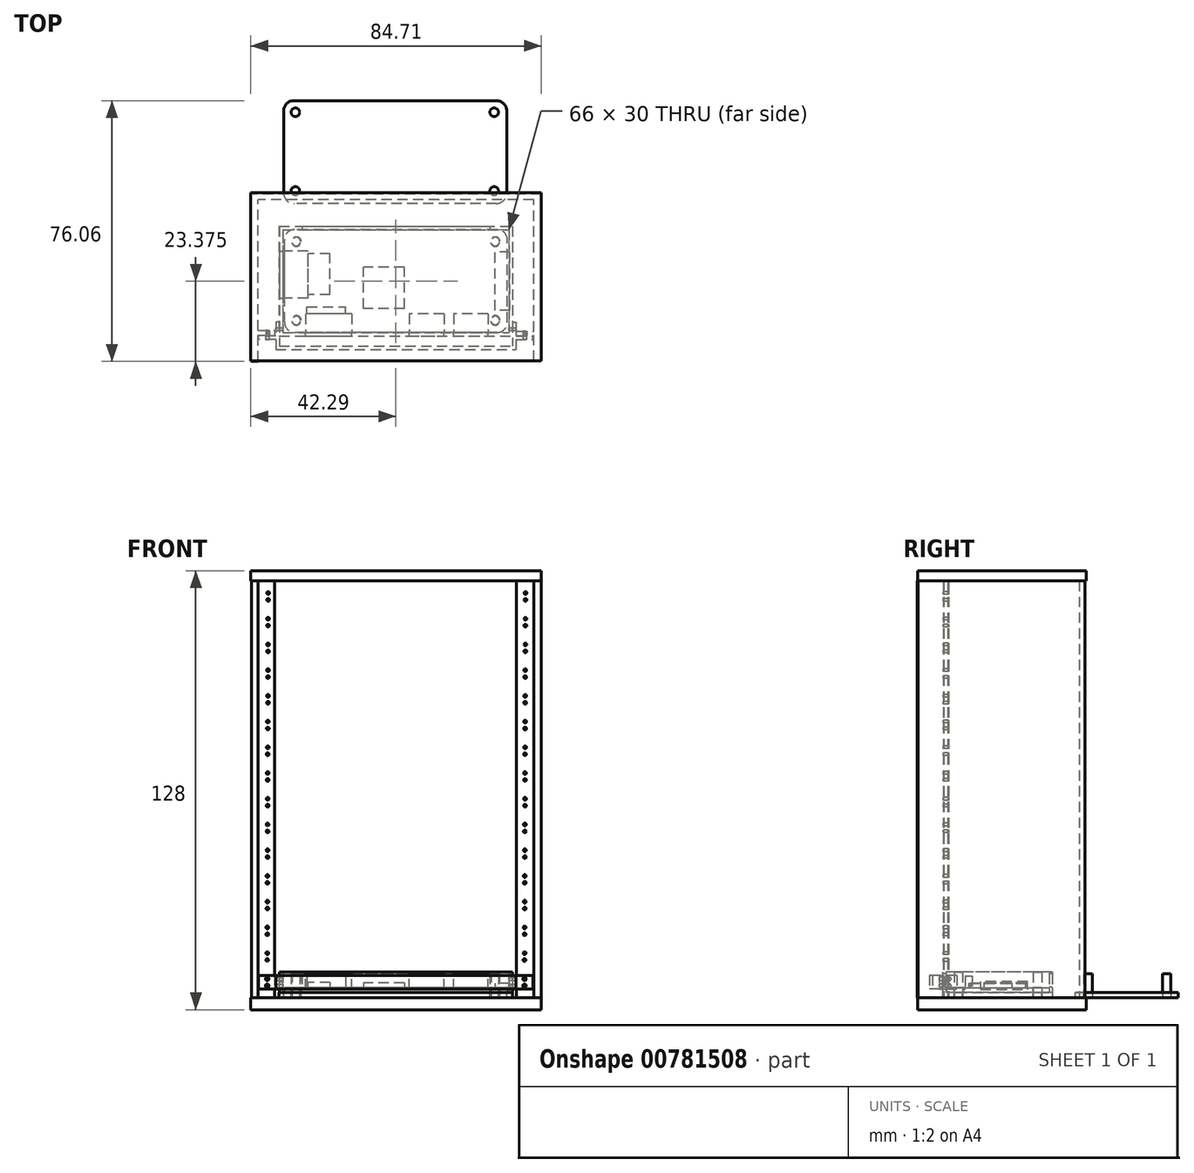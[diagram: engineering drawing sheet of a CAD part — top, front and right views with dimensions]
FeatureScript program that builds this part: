
annotation { "Feature Type Name" : "Feature", "Feature Type Description" : "" }
export const myFeature = defineFeature(function(context is Context, id is Id, definition is map)
    precondition{}
    {
        {
            var Q0;
            Q0=qCreatedBy(makeId("Top.planeOp"),FACE);
            var sketch = newSketch(context, id + "F0", { "sketchPlane" : qUnion([Q0])});
            skLineSegment(sketch, "E0.bottom", {"start": v(29.5, -15) * mm, "end": v(-29.5, -15) * mm});
            skLineSegment(sketch, "E0.top", {"start": v(29.5, 15) * mm, "end": v(-29.5, 15) * mm});
            skLineSegment(sketch, "E0.left", {"start": v(32.5, -12) * mm, "end": v(32.5, 12) * mm});
            skLineSegment(sketch, "E0.right", {"start": v(-32.5, -12) * mm, "end": v(-32.5, 12) * mm});
            skPoint(sketch, "E0.middle", {"position": v(0, 0) * mm});
            skCircle(sketch, "E1", {"center": v(-28.98, 11.47) * mm, "radius": 1.38 * mm});
            skCircle(sketch, "E2", {"center": v(28.98, 11.47) * mm, "radius": 1.38 * mm});
            skCircle(sketch, "E3", {"center": v(-28.98, -11.47) * mm, "radius": 1.38 * mm});
            skCircle(sketch, "E4", {"center": v(28.98, -11.47) * mm, "radius": 1.38 * mm});
            skPoint(sketch, "E5.visualSharp", {"position": v(-32.5, 15) * mm});
            skArc(sketch, "E5.filletArc", {"start": v(-29.5, 15) * mm, "mid": v(-31.62, 14.12) * mm, "end": v(-32.5, 12) * mm});
            skPoint(sketch, "E6.visualSharp", {"position": v(32.5, 15) * mm});
            skArc(sketch, "E6.filletArc", {"start": v(32.5, 12) * mm, "mid": v(31.62, 14.12) * mm, "end": v(29.5, 15) * mm});
            skPoint(sketch, "E7.visualSharp", {"position": v(32.5, -15) * mm});
            skArc(sketch, "E7.filletArc", {"start": v(29.5, -15) * mm, "mid": v(31.62, -14.12) * mm, "end": v(32.5, -12) * mm});
            skPoint(sketch, "E8.visualSharp", {"position": v(-32.5, -15) * mm});
            skArc(sketch, "E8.filletArc", {"start": v(-32.5, -12) * mm, "mid": v(-31.62, -14.12) * mm, "end": v(-29.5, -15) * mm});
            skSolve(sketch);
        }
        {
            var Q0;
            Q0=qSketchRegion(id+"F0",true);
            extrude(context, id + "F1", {"entities" : qUnion([Q0]), "depth" : 1.4 * mm});
        }
        {
            var Q0;
            Q0=makeQuery(id+"F1.opExtrude","CAP_FACE",FACE,{"disambiguationData":[OSD([sQuery(id+"F0.wireOp",EDGE,"E0.bottom"),sQuery(id+"F0.wireOp",EDGE,"E0.top"),sQuery(id+"F0.wireOp",EDGE,"E0.left"),sQuery(id+"F0.wireOp",EDGE,"E0.right"),sQuery(id+"F0.wireOp",EDGE,"E1"),sQuery(id+"F0.wireOp",EDGE,"E2"),sQuery(id+"F0.wireOp",EDGE,"E3"),sQuery(id+"F0.wireOp",EDGE,"E4"),sQuery(id+"F0.wireOp",EDGE,"E5.filletArc"),sQuery(id+"F0.wireOp",EDGE,"E6.filletArc"),sQuery(id+"F0.wireOp",EDGE,"E7.filletArc"),sQuery(id+"F0.wireOp",EDGE,"E8.filletArc")])],"isStart":false});
            var sketch = newSketch(context, id + "F2", { "sketchPlane" : qUnion([Q0])});
            skLineSegment(sketch, "E9.bottom", {"start": v(2.5, -8) * mm, "end": v(-9.5, -8) * mm});
            skLineSegment(sketch, "E9.top", {"start": v(2.5, 4) * mm, "end": v(-9.5, 4) * mm});
            skLineSegment(sketch, "E9.left", {"start": v(2.5, -8) * mm, "end": v(2.5, 4) * mm});
            skLineSegment(sketch, "E9.right", {"start": v(-9.5, -8) * mm, "end": v(-9.5, 4) * mm});
            skPoint(sketch, "E9.middle", {"position": v(-3.5, -2) * mm});
            skLineSegment(sketch, "E10.bottom", {"start": v(33.25, -8.5) * mm, "end": v(28.85, -8.5) * mm});
            skLineSegment(sketch, "E10.top", {"start": v(33.25, 8.5) * mm, "end": v(28.85, 8.5) * mm});
            skLineSegment(sketch, "E10.left", {"start": v(33.25, -8.5) * mm, "end": v(33.25, 8.5) * mm});
            skLineSegment(sketch, "E10.right", {"start": v(28.85, -8.5) * mm, "end": v(28.85, 8.5) * mm});
            skPoint(sketch, "E10.middle", {"position": v(31.05, 0) * mm});
            skPoint(sketch, "E11", {"position": v(32.5, 0) * mm});
            skLineSegment(sketch, "E12.bottom", {"start": v(-19.2, -4) * mm, "end": v(-34.6, -4) * mm});
            skLineSegment(sketch, "E12.top", {"start": v(-19.2, 8) * mm, "end": v(-34.6, 8) * mm});
            skLineSegment(sketch, "E12.left", {"start": v(-19.2, -4) * mm, "end": v(-19.2, 8) * mm});
            skLineSegment(sketch, "E12.right", {"start": v(-34.6, -4) * mm, "end": v(-34.6, 8) * mm});
            skPoint(sketch, "E12.middle", {"position": v(-26.9, 2) * mm});
            skLineSegment(sketch, "E13.bottom", {"start": v(-25.9, -15) * mm, "end": v(-14.7, -15) * mm});
            skLineSegment(sketch, "E13.top", {"start": v(-25.9, -7.5) * mm, "end": v(-14.7, -7.5) * mm});
            skLineSegment(sketch, "E13.left", {"start": v(-25.9, -15) * mm, "end": v(-25.9, -7.5) * mm});
            skLineSegment(sketch, "E13.right", {"start": v(-14.7, -15) * mm, "end": v(-14.7, -7.5) * mm});
            skLineSegment(sketch, "E14.bottom", {"start": v(5, -16.3) * mm, "end": v(13, -16.3) * mm});
            skLineSegment(sketch, "E14.top", {"start": v(5, -10.6) * mm, "end": v(13, -10.6) * mm});
            skLineSegment(sketch, "E14.left", {"start": v(5, -16.3) * mm, "end": v(5, -10.6) * mm});
            skLineSegment(sketch, "E14.right", {"start": v(13, -16.3) * mm, "end": v(13, -10.6) * mm});
            skLineSegment(sketch, "E15.bottom", {"start": v(17.9, -16.3) * mm, "end": v(25.9, -16.3) * mm});
            skLineSegment(sketch, "E15.top", {"start": v(17.9, -10.6) * mm, "end": v(25.9, -10.6) * mm});
            skLineSegment(sketch, "E15.left", {"start": v(17.9, -16.3) * mm, "end": v(17.9, -10.6) * mm});
            skLineSegment(sketch, "E15.right", {"start": v(25.9, -16.3) * mm, "end": v(25.9, -10.6) * mm});
            skSolve(sketch);
        }
        {
            var Q0;
            Q0=makeQuery(id+"F2.imprint","IMPRINT",FACE,{"disambiguationData":[TD([[makeQuery(id+"F2.imprint","IMPRINT",EDGE,{"derivedFrom":sQuery(id+"F2.wireOp",EDGE,"E9.bottom")}),-1.0]])]});
            extrude(context, id + "F3", {"entities" : qUnion([Q0]), "depth" : 1.4 * mm});
        }
        {
            var Q0;
            Q0=makeQuery(id+"F2.imprint","IMPRINT",FACE,{"disambiguationData":[TD([[makeQuery(id+"F2.imprint","IMPRINT",EDGE,{"derivedFrom":sQuery(id+"F2.wireOp",EDGE,"E13.bottom")}),-1.0]])]});
            extrude(context, id + "F4", {"entities" : qUnion([Q0]), "depth" : (4.8 - 1.4) * mm});
        }
        {
            var Q0;
            {var subQ0=sQuery(id+"F2.wireOp",EDGE,"E14.top");Q0=makeQuery(id+"F2.imprint","IMPRINT",FACE,{"disambiguationData":[TD([[makeQuery(id+"F2.imprint","IMPRINT",EDGE,{"derivedFrom":subQ0}),-1.0]])]});}
            var Q1;
            {var subQ0=sQuery(id+"F2.wireOp",EDGE,"E15.top");Q1=makeQuery(id+"F2.imprint","IMPRINT",FACE,{"disambiguationData":[TD([[makeQuery(id+"F2.imprint","IMPRINT",EDGE,{"derivedFrom":subQ0}),-1.0]])]});}
            var Q2;
            {var subQ0=sQuery(id+"F2.wireOp",EDGE,"E15.bottom");Q2=makeQuery(id+"F2.imprint","IMPRINT",FACE,{"disambiguationData":[TD([[makeQuery(id+"F2.imprint","IMPRINT",EDGE,{"derivedFrom":subQ0}),1.0]])]});}
            var Q3;
            {var subQ0=sQuery(id+"F2.wireOp",EDGE,"E14.bottom");Q3=makeQuery(id+"F2.imprint","IMPRINT",FACE,{"disambiguationData":[TD([[makeQuery(id+"F2.imprint","IMPRINT",EDGE,{"derivedFrom":subQ0}),1.0]])]});}
            extrude(context, id + "F5", {"entities" : qUnion([Q0, Q1, Q2, Q3]), "depth" : (4.25 - 1.4) * mm});
        }
        {
            var Q0;
            {var subQ0=sQuery(id+"F2.wireOp",EDGE,"E10.right");Q0=makeQuery(id+"F2.imprint","IMPRINT",FACE,{"disambiguationData":[TD([[makeQuery(id+"F2.imprint","IMPRINT",EDGE,{"derivedFrom":subQ0}),-1.0]])]});}
            var Q1;
            {var subQ0=sQuery(id+"F2.wireOp",EDGE,"E10.left");Q1=makeQuery(id+"F2.imprint","IMPRINT",FACE,{"disambiguationData":[TD([[makeQuery(id+"F2.imprint","IMPRINT",EDGE,{"derivedFrom":subQ0}),1.0]])]});}
            extrude(context, id + "F6", {"entities" : qUnion([Q0, Q1]), "depth" : (2.75 - 1.4) * mm});
        }
        {
            var Q0;
            {var subQ0=sQuery(id+"F2.wireOp",EDGE,"E12.right");Q0=makeQuery(id+"F2.imprint","IMPRINT",FACE,{"disambiguationData":[TD([[makeQuery(id+"F2.imprint","IMPRINT",EDGE,{"derivedFrom":subQ0}),-1.0]])]});}
            var Q1;
            {var subQ0=sQuery(id+"F2.wireOp",EDGE,"E12.left");Q1=makeQuery(id+"F2.imprint","IMPRINT",FACE,{"disambiguationData":[TD([[makeQuery(id+"F2.imprint","IMPRINT",EDGE,{"derivedFrom":subQ0}),1.0]])]});}
            extrude(context, id + "F7", {"entities" : qUnion([Q0, Q1]), "depth" : (2.9 - 1.4) * mm});
        }
        {
            var Q0;
            Q0=qCreatedBy(makeId("Top.planeOp"),FACE);
            var sketch = newSketch(context, id + "F8", { "sketchPlane" : qUnion([Q0])});
            skLineSegment(sketch, "E16.bottom", {"start": v(29.3, 22.6) * mm, "end": v(-29.7, 22.6) * mm});
            skLineSegment(sketch, "E16.top", {"start": v(29.3, 52.6) * mm, "end": v(-29.7, 52.6) * mm});
            skLineSegment(sketch, "E16.left", {"start": v(32.3, 25.6) * mm, "end": v(32.3, 49.6) * mm});
            skLineSegment(sketch, "E16.right", {"start": v(-32.7, 25.6) * mm, "end": v(-32.7, 49.6) * mm});
            skPoint(sketch, "E16.middle", {"position": v(-0.2, 37.6) * mm});
            skCircle(sketch, "E17", {"center": v(-29.3, 49.2) * mm, "radius": 1.25 * mm});
            skCircle(sketch, "E18", {"center": v(28.65, 49.2) * mm, "radius": 1.25 * mm});
            skCircle(sketch, "E19", {"center": v(-29.3, 26.25) * mm, "radius": 1.25 * mm});
            skCircle(sketch, "E20", {"center": v(28.65, 26.25) * mm, "radius": 1.25 * mm});
            skPoint(sketch, "E21.visualSharp", {"position": v(-32.7, 52.6) * mm});
            skArc(sketch, "E21.filletArc", {"start": v(-29.7, 52.6) * mm, "mid": v(-31.82, 51.72) * mm, "end": v(-32.7, 49.6) * mm});
            skPoint(sketch, "E22.visualSharp", {"position": v(32.3, 52.6) * mm});
            skArc(sketch, "E22.filletArc", {"start": v(32.3, 49.6) * mm, "mid": v(31.42, 51.72) * mm, "end": v(29.3, 52.6) * mm});
            skPoint(sketch, "E23.visualSharp", {"position": v(32.3, 22.6) * mm});
            skArc(sketch, "E23.filletArc", {"start": v(29.3, 22.6) * mm, "mid": v(31.42, 23.48) * mm, "end": v(32.3, 25.6) * mm});
            skPoint(sketch, "E24.visualSharp", {"position": v(-32.7, 22.6) * mm});
            skArc(sketch, "E24.filletArc", {"start": v(-32.7, 25.6) * mm, "mid": v(-31.82, 23.48) * mm, "end": v(-29.7, 22.6) * mm});
            skSolve(sketch);
        }
        {
            var Q0;
            Q0=makeQuery(id+"F8.imprint","IMPRINT",FACE,{"disambiguationData":[TD([[makeQuery(id+"F8.imprint","IMPRINT",EDGE,{"derivedFrom":sQuery(id+"F8.wireOp",EDGE,"E19")}),1.0]])]});
            var Q1;
            Q1=makeQuery(id+"F8.imprint","IMPRINT",FACE,{"disambiguationData":[TD([[makeQuery(id+"F8.imprint","IMPRINT",EDGE,{"derivedFrom":sQuery(id+"F8.wireOp",EDGE,"E17")}),1.0]])]});
            var Q2;
            Q2=makeQuery(id+"F8.imprint","IMPRINT",FACE,{"disambiguationData":[TD([[makeQuery(id+"F8.imprint","IMPRINT",EDGE,{"derivedFrom":sQuery(id+"F8.wireOp",EDGE,"E18")}),1.0]])]});
            var Q3;
            Q3=makeQuery(id+"F8.imprint","IMPRINT",FACE,{"disambiguationData":[TD([[makeQuery(id+"F8.imprint","IMPRINT",EDGE,{"derivedFrom":sQuery(id+"F8.wireOp",EDGE,"E20")}),1.0]])]});
            var Q4;
            Q4=sQuery(id+"F8.wireOp",EDGE,"E17");
            var Q5;
            Q5=sQuery(id+"F8.wireOp",EDGE,"E19");
            var Q6;
            Q6=sQuery(id+"F8.wireOp",EDGE,"E18");
            var Q7;
            Q7=sQuery(id+"F8.wireOp",EDGE,"E20");
            extrude(context, id + "F9", {"entities" : qUnion([Q0, Q1, Q2, Q3]), "surfaceEntities" : qUnion([Q4, Q5, Q6, Q7]), "depth" : 5.5 * mm, "offsetDistance" : 25 * mm, "hasSecondDirection" : true, "secondDirectionOppositeDirection" : true, "secondDirectionDepth" : 1.5 * mm});
        }
        {
            var Q0;
            Q0 = qSketchRegion(id + "F8", true);
            extrude(context, id + "F10", {"entities" : qUnion([Q0]), "depth" : 0 * mm, "offsetDistance" : 25 * mm, "hasSecondDirection" : true, "secondDirectionOppositeDirection" : true, "secondDirectionDepth" : 1.5 * mm});
        }
        {
            var Q0;
            Q0=qCreatedBy(makeId("Top.planeOp"),FACE);
            var sketch = newSketch(context, id + "F11", { "sketchPlane" : qUnion([Q0])});
            skLineSegment(sketch, "E25.bottom", {"start": v(-34, 15.91) * mm, "end": v(34, 15.91) * mm});
            skLineSegment(sketch, "E25.top", {"start": v(-34, -16.09) * mm, "end": v(34, -16.09) * mm});
            skLineSegment(sketch, "E25.left", {"start": v(-34, 15.91) * mm, "end": v(-34, -16.09) * mm});
            skLineSegment(sketch, "E25.right", {"start": v(34, 15.91) * mm, "end": v(34, -16.09) * mm});
            skLineSegment(sketch, "E26.bottom", {"start": v(-33, 14.91) * mm, "end": v(33, 14.91) * mm});
            skLineSegment(sketch, "E26.top", {"start": v(-33, -15.09) * mm, "end": v(33, -15.09) * mm});
            skLineSegment(sketch, "E26.left", {"start": v(-33, 14.91) * mm, "end": v(-33, -15.09) * mm});
            skLineSegment(sketch, "E26.right", {"start": v(33, 14.91) * mm, "end": v(33, -15.09) * mm});
            skPoint(sketch, "E27", {"position": v(0, -15.09) * mm});
            skPoint(sketch, "E28", {"position": v(0, -16.09) * mm});
            skPoint(sketch, "E29", {"position": v(0, 14.91) * mm});
            skPoint(sketch, "E30", {"position": v(0, 15.91) * mm});
            skPoint(sketch, "E31", {"position": v(-34, -0.09) * mm});
            skPoint(sketch, "E32", {"position": v(-33, -0.09) * mm});
            skPoint(sketch, "E33", {"position": v(33, -0.09) * mm});
            skPoint(sketch, "E34", {"position": v(34, -0.09) * mm});
            skSolve(sketch);
        }
        {
            var Q0;
            Q0=qCreatedBy(makeId("Top.planeOp"),FACE);
            var sketch = newSketch(context, id + "F12", { "sketchPlane" : qUnion([Q0])});
            skLineSegment(sketch, "E35.bottom", {"start": v(-26.34, -17.54) * mm, "end": v(-12.84, -17.54) * mm});
            skLineSegment(sketch, "E35.top", {"start": v(-26.34, -9.55) * mm, "end": v(-12.84, -9.55) * mm});
            skLineSegment(sketch, "E35.left", {"start": v(-26.34, -17.54) * mm, "end": v(-26.34, -9.55) * mm});
            skLineSegment(sketch, "E35.right", {"start": v(-12.84, -17.54) * mm, "end": v(-12.84, -9.55) * mm});
            skLineSegment(sketch, "E36.bottom", {"start": v(3.84, -17.54) * mm, "end": v(14.02, -17.54) * mm});
            skLineSegment(sketch, "E36.top", {"start": v(3.84, -9.55) * mm, "end": v(14.02, -9.55) * mm});
            skLineSegment(sketch, "E36.left", {"start": v(3.84, -17.54) * mm, "end": v(3.84, -9.55) * mm});
            skLineSegment(sketch, "E36.right", {"start": v(14.02, -17.54) * mm, "end": v(14.02, -9.55) * mm});
            skLineSegment(sketch, "E37.bottom", {"start": v(16.87, -17.41) * mm, "end": v(26.88, -17.41) * mm});
            skLineSegment(sketch, "E37.top", {"start": v(16.87, -9.55) * mm, "end": v(26.88, -9.55) * mm});
            skLineSegment(sketch, "E37.left", {"start": v(16.87, -17.41) * mm, "end": v(16.87, -9.55) * mm});
            skLineSegment(sketch, "E37.right", {"start": v(26.88, -17.41) * mm, "end": v(26.88, -9.55) * mm});
            skSolve(sketch);
        }
        {
            var Q0;
            Q0 = qSketchRegion(id + "F11", true);
            extrude(context, id + "F13", {"entities" : qUnion([Q0]), "depth" : 6 * mm, "offsetDistance" : 25 * mm});
        }
        {
            var Q0;
            Q0=qCreatedBy(makeId("Top.planeOp"),FACE);
            var sketch = newSketch(context, id + "F14", { "sketchPlane" : qUnion([Q0])});
            skLineSegment(sketch, "E38.bottom", {"start": v(-35.27, 8.67) * mm, "end": v(-25.56, 8.67) * mm});
            skLineSegment(sketch, "E38.top", {"start": v(-35.27, -5) * mm, "end": v(-25.56, -5) * mm});
            skLineSegment(sketch, "E38.left", {"start": v(-35.27, 8.67) * mm, "end": v(-35.27, -5) * mm});
            skLineSegment(sketch, "E38.right", {"start": v(-25.56, 8.67) * mm, "end": v(-25.56, -5) * mm});
            skSolve(sketch);
        }
        {
            var Q0;
            Q0=qCreatedBy(makeId("Top.planeOp"),FACE);
            var sketch = newSketch(context, id + "F15", { "sketchPlane" : qUnion([Q0])});
            skLineSegment(sketch, "E39.bottom", {"start": v(-27.35, 17.47) * mm, "end": v(27.37, 17.47) * mm});
            skLineSegment(sketch, "E39.top", {"start": v(-27.35, 9.27) * mm, "end": v(27.37, 9.27) * mm});
            skLineSegment(sketch, "E39.left", {"start": v(-27.35, 17.47) * mm, "end": v(-27.35, 9.27) * mm});
            skLineSegment(sketch, "E39.right", {"start": v(27.37, 17.47) * mm, "end": v(27.37, 9.27) * mm});
            skSolve(sketch);
        }
        {
            var Q0;
            Q0 = qSketchRegion(id + "F14", true);
            extrude(context, id + "F16", {"entities" : qUnion([Q0]), "operationType" : NewBodyOperationType.REMOVE, "depth" : 3.2 * mm, "offsetDistance" : 25 * mm, "hasSecondDirection" : true, "secondDirectionOppositeDirection" : false, "secondDirectionDepth" : 0.9 * mm});
        }
        {
            var Q0;
            Q0 = qSketchRegion(id + "F12", true);
            extrude(context, id + "F17", {"entities" : qUnion([Q0]), "operationType" : NewBodyOperationType.REMOVE, "depth" : 5.6 * mm, "offsetDistance" : 25 * mm, "hasSecondDirection" : true, "secondDirectionOppositeDirection" : false, "secondDirectionDepth" : 1 * mm});
        }
        {
            var Q0;
            Q0 = qSketchRegion(id + "F15", true);
            extrude(context, id + "F18", {"entities" : qUnion([Q0]), "operationType" : NewBodyOperationType.REMOVE, "depth" : 5.5 * mm, "offsetDistance" : 25 * mm, "hasSecondDirection" : true, "secondDirectionOppositeDirection" : false, "secondDirectionDepth" : 1.5 * mm});
        }
        {
            var Q0;
            Q0=qCreatedBy(makeId("Top.planeOp"),FACE);
            var sketch = newSketch(context, id + "F19", { "sketchPlane" : qUnion([Q0])});
            skLineSegment(sketch, "E40.bottom", {"start": v(-34.03, 16) * mm, "end": v(33.97, 16) * mm});
            skLineSegment(sketch, "E40.top", {"start": v(-34.03, -16) * mm, "end": v(33.97, -16) * mm});
            skLineSegment(sketch, "E40.left", {"start": v(-34.03, 16) * mm, "end": v(-34.03, -16) * mm});
            skLineSegment(sketch, "E40.right", {"start": v(33.97, 16) * mm, "end": v(33.97, -16) * mm});
            skCircle(sketch, "E41", {"center": v(-29.03, 11.5) * mm, "radius": 1.25 * mm});
            skCircle(sketch, "E42", {"center": v(28.97, 11.5) * mm, "radius": 1.25 * mm});
            skCircle(sketch, "E43", {"center": v(28.97, -11.5) * mm, "radius": 1.25 * mm});
            skCircle(sketch, "E44", {"center": v(-29.03, -11.5) * mm, "radius": 1.25 * mm});
            skSolve(sketch);
        }
        {
            var Q0;
            Q0=makeQuery(id+"F19.imprint","IMPRINT",FACE,{"disambiguationData":[TD([[makeQuery(id+"F19.imprint","IMPRINT",EDGE,{"derivedFrom":sQuery(id+"F19.wireOp",EDGE,"E44")}),1.0]])]});
            var Q1;
            Q1=makeQuery(id+"F19.imprint","IMPRINT",FACE,{"disambiguationData":[TD([[makeQuery(id+"F19.imprint","IMPRINT",EDGE,{"derivedFrom":sQuery(id+"F19.wireOp",EDGE,"E41")}),1.0]])]});
            var Q2;
            Q2=makeQuery(id+"F19.imprint","IMPRINT",FACE,{"disambiguationData":[TD([[makeQuery(id+"F19.imprint","IMPRINT",EDGE,{"derivedFrom":sQuery(id+"F19.wireOp",EDGE,"E42")}),1.0]])]});
            var Q3;
            Q3=makeQuery(id+"F19.imprint","IMPRINT",FACE,{"disambiguationData":[TD([[makeQuery(id+"F19.imprint","IMPRINT",EDGE,{"derivedFrom":sQuery(id+"F19.wireOp",EDGE,"E43")}),1.0]])]});
            extrude(context, id + "F20", {"entities" : qUnion([Q0, Q1, Q2, Q3]), "depth" : 6 * mm, "offsetDistance" : 25 * mm, "hasSecondDirection" : true, "secondDirectionOppositeDirection" : true, "secondDirectionDepth" : 1.5 * mm});
        }
        {
            var Q0;
            Q0 = qSketchRegion(id + "F19", true);
            extrude(context, id + "F21", {"entities" : qUnion([Q0]), "oppositeDirection" : true, "depth" : 1.5 * mm, "offsetDistance" : 25 * mm});
        }
        {
            var Q0;
            Q0=qCreatedBy(makeId("Top.planeOp"),FACE);
            var sketch = newSketch(context, id + "F22", { "sketchPlane" : qUnion([Q0])});
            skLineSegment(sketch, "E45.bottom", {"start": v(-34.01, -12.01) * mm, "end": v(-35.01, -12.01) * mm});
            skLineSegment(sketch, "E45.top", {"start": v(-34.01, -19.01) * mm, "end": v(-35.01, -19.01) * mm});
            skLineSegment(sketch, "E45.left", {"start": v(-34.01, -12.01) * mm, "end": v(-34.01, -19.01) * mm});
            skLineSegment(sketch, "E45.right", {"start": v(-35.01, -12.01) * mm, "end": v(-35.01, -19.01) * mm});
            skLineSegment(sketch, "E46.bottom", {"start": v(-35.01, -17.01) * mm, "end": v(-40.01, -17.01) * mm});
            skLineSegment(sketch, "E46.top", {"start": v(-35.01, -16.01) * mm, "end": v(-40.01, -16.01) * mm});
            skLineSegment(sketch, "E46.left", {"start": v(-35.01, -17.01) * mm, "end": v(-35.01, -16.01) * mm});
            skLineSegment(sketch, "E46.right", {"start": v(-40.01, -17.01) * mm, "end": v(-40.01, -16.01) * mm});
            skLineSegment(sketch, "E47.MirrorCS", {"start": v(34.99, -17.01) * mm, "end": v(34.99, -16.01) * mm});
            skLineSegment(sketch, "E48.MirrorCS", {"start": v(33.99, -12.01) * mm, "end": v(34.99, -12.01) * mm});
            skLineSegment(sketch, "E49.MirrorCS", {"start": v(39.99, -17.01) * mm, "end": v(39.99, -16.01) * mm});
            skLineSegment(sketch, "E50.MirrorCS", {"start": v(33.99, -19.01) * mm, "end": v(34.99, -19.01) * mm});
            skLineSegment(sketch, "E51.MirrorCS", {"start": v(34.99, -17.01) * mm, "end": v(39.99, -17.01) * mm});
            skLineSegment(sketch, "E52.MirrorCS", {"start": v(34.99, -16.01) * mm, "end": v(39.99, -16.01) * mm});
            skLineSegment(sketch, "E53.MirrorCS", {"start": v(33.99, -12.01) * mm, "end": v(33.99, -19.01) * mm});
            skLineSegment(sketch, "E54.MirrorCS", {"start": v(34.99, -12.01) * mm, "end": v(34.99, -19.01) * mm});
            skLineSegment(sketch, "E55.bottom", {"start": v(-35.01, -19.01) * mm, "end": v(34.99, -19.01) * mm});
            skLineSegment(sketch, "E55.top", {"start": v(-35.01, -20.01) * mm, "end": v(34.99, -20.01) * mm});
            skLineSegment(sketch, "E55.left", {"start": v(-35.01, -19.01) * mm, "end": v(-35.01, -20.01) * mm});
            skLineSegment(sketch, "E55.right", {"start": v(34.99, -19.01) * mm, "end": v(34.99, -20.01) * mm});
            skSolve(sketch);
        }
        {
            var Q0;
            Q0=makeQuery(id+"F22.imprint","IMPRINT",FACE,{"disambiguationData":[TD([[makeQuery(id+"F22.imprint","IMPRINT",EDGE,{"derivedFrom":sQuery(id+"F22.wireOp",EDGE,"E46.bottom")}),-1.0]])]});
            var Q1;
            {var subQ4=sQuery(id+"F22.wireOp",EDGE,"E45.bottom");Q1=makeQuery(id+"F22.imprint","IMPRINT",FACE,{"disambiguationData":[TD([[makeQuery(id+"F22.imprint","IMPRINT",EDGE,{"derivedFrom":subQ4}),1.0]])]});}
            var Q2;
            Q2=makeQuery(id+"F22.imprint","IMPRINT",FACE,{"disambiguationData":[TD([[makeQuery(id+"F22.imprint","IMPRINT",EDGE,{"derivedFrom":sQuery(id+"F22.wireOp",EDGE,"E55.top")}),1.0]])]});
            var Q3;
            Q3=makeQuery(id+"F22.imprint","IMPRINT",FACE,{"disambiguationData":[TD([[makeQuery(id+"F22.imprint","IMPRINT",EDGE,{"derivedFrom":sQuery(id+"F22.wireOp",EDGE,"E49.MirrorCS")}),1.0]])]});
            var Q4;
            {var subQ4=sQuery(id+"F22.wireOp",EDGE,"E48.MirrorCS");Q4=makeQuery(id+"F22.imprint","IMPRINT",FACE,{"disambiguationData":[TD([[makeQuery(id+"F22.imprint","IMPRINT",EDGE,{"derivedFrom":subQ4}),-1.0]])]});}
            extrude(context, id + "F23", {"entities" : qUnion([Q0, Q1, Q2, Q3, Q4]), "depth" : 5 * mm, "offsetDistance" : 25 * mm, "hasSecondDirection" : true, "secondDirectionOppositeDirection" : false, "secondDirectionDepth" : 1 * mm});
        }
        {
            var Q0;
            Q0=makeQuery(id+"F23.opExtrude","SWEPT_FACE",FACE,{"disambiguationData":[OSD([sQuery(id+"F22.wireOp",EDGE,"E46.bottom")])]});
            var sketch = newSketch(context, id + "F24", { "sketchPlane" : qUnion([Q0])});
            skCircle(sketch, "E56", {"center": v(-37.51, 4) * mm, "radius": 0.5 * mm});
            skCircle(sketch, "E57", {"center": v(-37.51, 2) * mm, "radius": 0.5 * mm});
            skSolve(sketch);
        }
        {
            var Q0;
            Q0=sQuery(id+"F24.wireOp",VERTEX,"E56.center");
            var Q1;
            Q1=sQuery(id+"F24.wireOp",VERTEX,"E57.center");
            var Q2;
            Q2=makeQuery(id+"F23.opExtrude","SWEPT_BODY",BODY,{"disambiguationData":[OSD([sQuery(id+"F22.wireOp",EDGE,"E45.bottom"),sQuery(id+"F22.wireOp",EDGE,"E45.left"),sQuery(id+"F22.wireOp",EDGE,"E45.right"),sQuery(id+"F22.wireOp",EDGE,"E46.bottom"),sQuery(id+"F22.wireOp",EDGE,"E46.top"),sQuery(id+"F22.wireOp",EDGE,"E46.right"),sQuery(id+"F22.wireOp",EDGE,"E48.MirrorCS"),sQuery(id+"F22.wireOp",EDGE,"E49.MirrorCS"),sQuery(id+"F22.wireOp",EDGE,"E51.MirrorCS"),sQuery(id+"F22.wireOp",EDGE,"E52.MirrorCS"),sQuery(id+"F22.wireOp",EDGE,"E53.MirrorCS"),sQuery(id+"F22.wireOp",EDGE,"E54.MirrorCS"),sQuery(id+"F22.wireOp",EDGE,"E55.bottom"),sQuery(id+"F22.wireOp",EDGE,"E55.top"),sQuery(id+"F22.wireOp",EDGE,"E55.left"),sQuery(id+"F22.wireOp",EDGE,"E55.right")])]});
            hole(context, id + "F25", {"style" : HoleStyle.SIMPLE, "endStyle" : HoleEndStyle.THROUGH, "holeDiameter" : 1 * mm, "majorDiameter" : 5 * mm, "isTappedThrough" : true, "tappedDepth" : 12 * mm, "tapClearance" : 3, "locations" : qUnion([Q0, Q1]), "scope" : qUnion([Q2])});
        }
        {
            var Q0;
            Q0=makeQuery(id+"F23.opExtrude","SWEPT_FACE",FACE,{"disambiguationData":[OSD([sQuery(id+"F22.wireOp",EDGE,"E51.MirrorCS")])]});
            var sketch = newSketch(context, id + "F26", { "sketchPlane" : qUnion([Q0])});
            skPoint(sketch, "E58", {"position": v(37.49, 4) * mm});
            skPoint(sketch, "E59", {"position": v(37.49, 2) * mm});
            skSolve(sketch);
        }
        {
            var Q0;
            Q0=sQuery(id+"F26.wireOp",VERTEX,"E59");
            var Q1;
            Q1=sQuery(id+"F26.wireOp",VERTEX,"E58");
            var Q2;
            Q2=makeQuery(id+"F23.opExtrude","SWEPT_BODY",BODY,{"disambiguationData":[OSD([sQuery(id+"F22.wireOp",EDGE,"E45.bottom"),sQuery(id+"F22.wireOp",EDGE,"E45.left"),sQuery(id+"F22.wireOp",EDGE,"E45.right"),sQuery(id+"F22.wireOp",EDGE,"E46.bottom"),sQuery(id+"F22.wireOp",EDGE,"E46.top"),sQuery(id+"F22.wireOp",EDGE,"E46.right"),sQuery(id+"F22.wireOp",EDGE,"E48.MirrorCS"),sQuery(id+"F22.wireOp",EDGE,"E49.MirrorCS"),sQuery(id+"F22.wireOp",EDGE,"E51.MirrorCS"),sQuery(id+"F22.wireOp",EDGE,"E52.MirrorCS"),sQuery(id+"F22.wireOp",EDGE,"E53.MirrorCS"),sQuery(id+"F22.wireOp",EDGE,"E54.MirrorCS"),sQuery(id+"F22.wireOp",EDGE,"E55.bottom"),sQuery(id+"F22.wireOp",EDGE,"E55.top"),sQuery(id+"F22.wireOp",EDGE,"E55.left"),sQuery(id+"F22.wireOp",EDGE,"E55.right")])]});
            hole(context, id + "F27", {"style" : HoleStyle.SIMPLE, "endStyle" : HoleEndStyle.THROUGH, "holeDiameter" : 1 * mm, "majorDiameter" : 5 * mm, "isTappedThrough" : true, "tappedDepth" : 12 * mm, "tapClearance" : 3, "locations" : qUnion([Q0, Q1]), "scope" : qUnion([Q2])});
        }
        {
            var Q0;
            Q0=makeQuery(id+"F23.opExtrude","SWEPT_FACE",FACE,{"disambiguationData":[OSD([sQuery(id+"F22.wireOp",EDGE,"E54.MirrorCS")])]});
            var sketch = newSketch(context, id + "F28", { "sketchPlane" : qUnion([Q0])});
            skPoint(sketch, "E60", {"position": v(-14.01, 4) * mm});
            skPoint(sketch, "E61", {"position": v(-14.01, 2) * mm});
            skSolve(sketch);
        }
        {
            var Q0;
            Q0=sQuery(id+"F28.wireOp",VERTEX,"E61");
            var Q1;
            Q1=sQuery(id+"F28.wireOp",VERTEX,"E60");
            var Q2;
            Q2=makeQuery(id+"F13.opExtrude","SWEPT_BODY",BODY,{"disambiguationData":[OSD([sQuery(id+"F11.wireOp",EDGE,"E25.bottom"),sQuery(id+"F11.wireOp",EDGE,"E25.top"),sQuery(id+"F11.wireOp",EDGE,"E25.left"),sQuery(id+"F11.wireOp",EDGE,"E25.right"),sQuery(id+"F11.wireOp",EDGE,"E26.bottom"),sQuery(id+"F11.wireOp",EDGE,"E26.top"),sQuery(id+"F11.wireOp",EDGE,"E26.left"),sQuery(id+"F11.wireOp",EDGE,"E26.right")])]});
            var Q3;
            Q3=makeQuery(id+"F23.opExtrude","SWEPT_BODY",BODY,{"disambiguationData":[OSD([sQuery(id+"F22.wireOp",EDGE,"E45.bottom"),sQuery(id+"F22.wireOp",EDGE,"E45.left"),sQuery(id+"F22.wireOp",EDGE,"E45.right"),sQuery(id+"F22.wireOp",EDGE,"E46.bottom"),sQuery(id+"F22.wireOp",EDGE,"E46.top"),sQuery(id+"F22.wireOp",EDGE,"E46.right"),sQuery(id+"F22.wireOp",EDGE,"E48.MirrorCS"),sQuery(id+"F22.wireOp",EDGE,"E49.MirrorCS"),sQuery(id+"F22.wireOp",EDGE,"E51.MirrorCS"),sQuery(id+"F22.wireOp",EDGE,"E52.MirrorCS"),sQuery(id+"F22.wireOp",EDGE,"E53.MirrorCS"),sQuery(id+"F22.wireOp",EDGE,"E54.MirrorCS"),sQuery(id+"F22.wireOp",EDGE,"E55.bottom"),sQuery(id+"F22.wireOp",EDGE,"E55.top"),sQuery(id+"F22.wireOp",EDGE,"E55.left"),sQuery(id+"F22.wireOp",EDGE,"E55.right")])]});
            var Q4;
            Q4=makeQuery(id+"F4.opExtrude","SWEPT_BODY",BODY,{"disambiguationData":[OSD([sQuery(id+"F2.wireOp",EDGE,"E13.bottom"),sQuery(id+"F2.wireOp",EDGE,"E13.top"),sQuery(id+"F2.wireOp",EDGE,"E13.left"),sQuery(id+"F2.wireOp",EDGE,"E13.right")])]});
            var Q5;
            Q5=makeQuery(id+"F5.opExtrude","SWEPT_BODY",BODY,{"disambiguationData":[OSD([sQuery(id+"F2.wireOp",EDGE,"E14.bottom"),sQuery(id+"F2.wireOp",EDGE,"E14.top"),sQuery(id+"F2.wireOp",EDGE,"E14.left"),sQuery(id+"F2.wireOp",EDGE,"E14.right")])]});
            var Q6;
            Q6=makeQuery(id+"F5.opExtrude","SWEPT_BODY",BODY,{"disambiguationData":[OSD([sQuery(id+"F2.wireOp",EDGE,"E15.bottom"),sQuery(id+"F2.wireOp",EDGE,"E15.top"),sQuery(id+"F2.wireOp",EDGE,"E15.left"),sQuery(id+"F2.wireOp",EDGE,"E15.right")])]});
            hole(context, id + "F29", {"style" : HoleStyle.SIMPLE, "endStyle" : HoleEndStyle.THROUGH, "holeDiameter" : .8 * mm, "majorDiameter" : 5 * mm, "isTappedThrough" : true, "tappedDepth" : 12 * mm, "tapClearance" : 3, "locations" : qUnion([Q0, Q1]), "scope" : qUnion([Q2, Q3, Q4, Q5, Q6])});
        }
        {
            var Q0;
            Q0=qCreatedBy(makeId("Top.planeOp"),FACE);
            var sketch = newSketch(context, id + "F30", { "sketchPlane" : qUnion([Q0])});
            skLineSegment(sketch, "E62.bottom", {"start": v(-40.19, -23.46) * mm, "end": v(-42.05, -23.46) * mm});
            skLineSegment(sketch, "E62.top", {"start": v(-40.19, 23.74) * mm, "end": v(-42.05, 23.74) * mm});
            skLineSegment(sketch, "E62.left", {"start": v(-40.19, -23.46) * mm, "end": v(-40.19, 23.74) * mm});
            skLineSegment(sketch, "E62.right", {"start": v(-42.05, -23.46) * mm, "end": v(-42.05, 23.74) * mm});
            skLineSegment(sketch, "E63.bottom", {"start": v(40.2, -23.26) * mm, "end": v(42.4, -23.26) * mm});
            skLineSegment(sketch, "E63.top", {"start": v(40.2, 23.74) * mm, "end": v(42.4, 23.74) * mm});
            skLineSegment(sketch, "E63.left", {"start": v(40.2, -23.26) * mm, "end": v(40.2, 23.74) * mm});
            skLineSegment(sketch, "E63.right", {"start": v(42.4, -23.26) * mm, "end": v(42.4, 23.74) * mm});
            skLineSegment(sketch, "E64.bottom", {"start": v(42.4, 23.74) * mm, "end": v(-42.05, 23.74) * mm});
            skLineSegment(sketch, "E64.top", {"start": v(42.4, 25.41) * mm, "end": v(-42.05, 25.41) * mm});
            skLineSegment(sketch, "E64.left", {"start": v(42.4, 23.74) * mm, "end": v(42.4, 25.41) * mm});
            skLineSegment(sketch, "E64.right", {"start": v(-42.05, 23.74) * mm, "end": v(-42.05, 25.41) * mm});
            skLineSegment(sketch, "E65.bottom", {"start": v(-40.19, -14.35) * mm, "end": v(-35.32, -14.35) * mm});
            skLineSegment(sketch, "E65.top", {"start": v(-40.19, -15.75) * mm, "end": v(-35.32, -15.75) * mm});
            skLineSegment(sketch, "E65.left", {"start": v(-40.19, -14.35) * mm, "end": v(-40.19, -15.75) * mm});
            skLineSegment(sketch, "E65.right", {"start": v(-35.32, -14.35) * mm, "end": v(-35.32, -15.75) * mm});
            skLineSegment(sketch, "E66.bottom", {"start": v(35.18, -15.86) * mm, "end": v(40.2, -15.86) * mm});
            skLineSegment(sketch, "E66.top", {"start": v(35.18, -14.66) * mm, "end": v(40.2, -14.66) * mm});
            skLineSegment(sketch, "E66.left", {"start": v(35.18, -15.86) * mm, "end": v(35.18, -14.66) * mm});
            skLineSegment(sketch, "E66.right", {"start": v(40.2, -15.86) * mm, "end": v(40.2, -14.66) * mm});
            skSolve(sketch);
        }
        {
            var Q0;
            Q0=makeQuery(id+"F30.imprint","IMPRINT",FACE,{"disambiguationData":[TD([[makeQuery(id+"F30.imprint","IMPRINT",EDGE,{"derivedFrom":sQuery(id+"F30.wireOp",EDGE,"E65.bottom")}),-1.0]])]});
            var Q1;
            {var subQ5=sQuery(id+"F30.wireOp",EDGE,"E62.bottom");Q1=makeQuery(id+"F30.imprint","IMPRINT",FACE,{"disambiguationData":[TD([[makeQuery(id+"F30.imprint","IMPRINT",EDGE,{"derivedFrom":subQ5}),-1.0]])]});}
            var Q2;
            Q2=makeQuery(id+"F30.imprint","IMPRINT",FACE,{"disambiguationData":[TD([[makeQuery(id+"F30.imprint","IMPRINT",EDGE,{"derivedFrom":sQuery(id+"F30.wireOp",EDGE,"E64.top")}),1.0]])]});
            var Q3;
            {var subQ5=sQuery(id+"F30.wireOp",EDGE,"E63.bottom");Q3=makeQuery(id+"F30.imprint","IMPRINT",FACE,{"disambiguationData":[TD([[makeQuery(id+"F30.imprint","IMPRINT",EDGE,{"derivedFrom":subQ5}),1.0]])]});}
            var Q4;
            Q4=makeQuery(id+"F30.imprint","IMPRINT",FACE,{"disambiguationData":[TD([[makeQuery(id+"F30.imprint","IMPRINT",EDGE,{"derivedFrom":sQuery(id+"F30.wireOp",EDGE,"E66.bottom")}),1.0]])]});
            extrude(context, id + "F31", {"entities" : qUnion([Q0, Q1, Q2, Q3, Q4]), "depth" : 120 * mm, "offsetDistance" : 25 * mm, "hasSecondDirection" : true, "secondDirectionOppositeDirection" : true, "secondDirectionDepth" : 1.5 * mm});
        }
        {
            var Q0;
            Q0=qCreatedBy(makeId("Top.planeOp"),FACE);
            var sketch = newSketch(context, id + "F32", { "sketchPlane" : qUnion([Q0])});
            skLineSegment(sketch, "E67.bottom", {"start": v(-42.3, 25.7) * mm, "end": v(42.42, 25.7) * mm});
            skLineSegment(sketch, "E67.top", {"start": v(-42.3, -23.34) * mm, "end": v(42.42, -23.34) * mm});
            skLineSegment(sketch, "E67.left", {"start": v(-42.3, 25.7) * mm, "end": v(-42.3, -23.34) * mm});
            skLineSegment(sketch, "E67.right", {"start": v(42.42, 25.7) * mm, "end": v(42.42, -23.34) * mm});
            skSolve(sketch);
        }
        {
            var Q0;
            Q0 = qSketchRegion(id + "F32", true);
            extrude(context, id + "F33", {"entities" : qUnion([Q0]), "oppositeDirection" : true, "depth" : 5 * mm, "offsetDistance" : 25 * mm, "hasSecondDirection" : true, "secondDirectionOppositeDirection" : true, "secondDirectionDepth" : 1.5 * mm});
        }
        {
            var Q0;
            Q0 = qSketchRegion(id + "F32", true);
            extrude(context, id + "F34", {"entities" : qUnion([Q0]), "operationType" : NewBodyOperationType.ADD, "depth" : 123 * mm, "offsetDistance" : 25 * mm, "hasSecondDirection" : true, "secondDirectionOppositeDirection" : false, "secondDirectionDepth" : 120 * mm});
        }
        {
            var Q0;
            Q0=makeQuery(id+"F31.opExtrude","SWEPT_FACE",FACE,{"disambiguationData":[OSD([sQuery(id+"F30.wireOp",EDGE,"E65.top")])]});
            var sketch = newSketch(context, id + "F35", { "sketchPlane" : qUnion([Q0])});
            skPoint(sketch, "E68", {"position": v(-37.51, 4) * mm});
            skPoint(sketch, "E69", {"position": v(-37.51, 2) * mm});
            skPoint(sketch, "E70", {"position": v(-37.48, 11.5) * mm});
            skPoint(sketch, "E71", {"position": v(-37.51, 9.5) * mm});
            skPoint(sketch, "E72", {"position": v(-37.48, 19) * mm});
            skPoint(sketch, "E73", {"position": v(-37.48, 17) * mm});
            skPoint(sketch, "E74", {"position": v(-37.44, 26.5) * mm});
            skPoint(sketch, "E75", {"position": v(-37.44, 24.5) * mm});
            skPoint(sketch, "E76", {"position": v(-37.44, 34) * mm});
            skPoint(sketch, "E77", {"position": v(-37.44, 32) * mm});
            skPoint(sketch, "E78", {"position": v(-37.4, 41.5) * mm});
            skPoint(sketch, "E79", {"position": v(-37.4, 39.5) * mm});
            skPoint(sketch, "E80", {"position": v(-37.4, 49) * mm});
            skPoint(sketch, "E81", {"position": v(-37.4, 47) * mm});
            skPoint(sketch, "E82", {"position": v(-37.37, 56.5) * mm});
            skPoint(sketch, "E83", {"position": v(-37.37, 54.5) * mm});
            skPoint(sketch, "E84", {"position": v(-37.37, 64) * mm});
            skPoint(sketch, "E85", {"position": v(-37.37, 62) * mm});
            skPoint(sketch, "E86", {"position": v(-37.33, 71.5) * mm});
            skPoint(sketch, "E87", {"position": v(-37.37, 69.5) * mm});
            skPoint(sketch, "E88", {"position": v(-37.33, 79) * mm});
            skPoint(sketch, "E89", {"position": v(-37.33, 77) * mm});
            skPoint(sketch, "E90", {"position": v(-37.3, 86.5) * mm});
            skPoint(sketch, "E91", {"position": v(-37.3, 84.5) * mm});
            skPoint(sketch, "E92", {"position": v(-37.3, 94) * mm});
            skPoint(sketch, "E93", {"position": v(-37.3, 92) * mm});
            skPoint(sketch, "E94", {"position": v(-37.25, 101.5) * mm});
            skPoint(sketch, "E95", {"position": v(-37.25, 99.5) * mm});
            skPoint(sketch, "E96", {"position": v(-37.25, 109) * mm});
            skPoint(sketch, "E97", {"position": v(-37.25, 107) * mm});
            skPoint(sketch, "E98", {"position": v(-37.22, 116.5) * mm});
            skPoint(sketch, "E99", {"position": v(-37.22, 114.5) * mm});
            skSolve(sketch);
        }
        {
            var Q0;
            Q0=sQuery(id+"F35.wireOp",VERTEX,"E80");
            var Q1;
            Q1=sQuery(id+"F35.wireOp",VERTEX,"E81");
            var Q2;
            Q2=sQuery(id+"F35.wireOp",VERTEX,"E83");
            var Q3;
            Q3=sQuery(id+"F35.wireOp",VERTEX,"E82");
            var Q4;
            Q4=sQuery(id+"F35.wireOp",VERTEX,"E85");
            var Q5;
            Q5=sQuery(id+"F35.wireOp",VERTEX,"E84");
            var Q6;
            Q6=sQuery(id+"F35.wireOp",VERTEX,"E98");
            var Q7;
            Q7=sQuery(id+"F35.wireOp",VERTEX,"E99");
            var Q8;
            Q8=sQuery(id+"F35.wireOp",VERTEX,"E96");
            var Q9;
            Q9=sQuery(id+"F35.wireOp",VERTEX,"E97");
            var Q10;
            Q10=sQuery(id+"F35.wireOp",VERTEX,"E94");
            var Q11;
            Q11=sQuery(id+"F35.wireOp",VERTEX,"E95");
            var Q12;
            Q12=sQuery(id+"F35.wireOp",VERTEX,"E92");
            var Q13;
            Q13=sQuery(id+"F35.wireOp",VERTEX,"E93");
            var Q14;
            Q14=sQuery(id+"F35.wireOp",VERTEX,"E90");
            var Q15;
            Q15=sQuery(id+"F35.wireOp",VERTEX,"E91");
            var Q16;
            Q16=sQuery(id+"F35.wireOp",VERTEX,"E88");
            var Q17;
            Q17=sQuery(id+"F35.wireOp",VERTEX,"E89");
            var Q18;
            Q18=sQuery(id+"F35.wireOp",VERTEX,"E86");
            var Q19;
            Q19=sQuery(id+"F35.wireOp",VERTEX,"E87");
            var Q20;
            Q20=sQuery(id+"F35.wireOp",VERTEX,"E78");
            var Q21;
            Q21=sQuery(id+"F35.wireOp",VERTEX,"E79");
            var Q22;
            Q22=sQuery(id+"F35.wireOp",VERTEX,"E76");
            var Q23;
            Q23=sQuery(id+"F35.wireOp",VERTEX,"E77");
            var Q24;
            Q24=sQuery(id+"F35.wireOp",VERTEX,"E74");
            var Q25;
            Q25=sQuery(id+"F35.wireOp",VERTEX,"E75");
            var Q26;
            Q26=sQuery(id+"F35.wireOp",VERTEX,"E72");
            var Q27;
            Q27=sQuery(id+"F35.wireOp",VERTEX,"E73");
            var Q28;
            Q28=sQuery(id+"F35.wireOp",VERTEX,"E70");
            var Q29;
            Q29=sQuery(id+"F35.wireOp",VERTEX,"E71");
            var Q30;
            Q30=sQuery(id+"F35.wireOp",VERTEX,"E68");
            var Q31;
            Q31=sQuery(id+"F35.wireOp",VERTEX,"E69");
            var Q32;
            Q32=makeQuery(id+"F31.opExtrude","SWEPT_BODY",BODY,{"disambiguationData":[OSD([sQuery(id+"F30.wireOp",EDGE,"E62.bottom"),sQuery(id+"F30.wireOp",EDGE,"E62.left"),sQuery(id+"F30.wireOp",EDGE,"E62.right"),sQuery(id+"F30.wireOp",EDGE,"E63.bottom"),sQuery(id+"F30.wireOp",EDGE,"E63.left"),sQuery(id+"F30.wireOp",EDGE,"E63.right"),sQuery(id+"F30.wireOp",EDGE,"E64.bottom"),sQuery(id+"F30.wireOp",EDGE,"E64.top"),sQuery(id+"F30.wireOp",EDGE,"E64.left"),sQuery(id+"F30.wireOp",EDGE,"E64.right"),sQuery(id+"F30.wireOp",EDGE,"E65.bottom"),sQuery(id+"F30.wireOp",EDGE,"E65.top"),sQuery(id+"F30.wireOp",EDGE,"E65.right"),sQuery(id+"F30.wireOp",EDGE,"E66.bottom"),sQuery(id+"F30.wireOp",EDGE,"E66.top"),sQuery(id+"F30.wireOp",EDGE,"E66.left")])]});
            hole(context, id + "F36", {"style" : HoleStyle.SIMPLE, "endStyle" : HoleEndStyle.BLIND, "holeDiameter" : .8 * mm, "majorDiameter" : 5 * mm, "holeDepth" : 2 * mm, "isTappedThrough" : true, "tappedDepth" : 12 * mm, "tapClearance" : 3, "locations" : qUnion([Q0, Q1, Q2, Q3, Q4, Q5, Q6, Q7, Q8, Q9, Q10, Q11, Q12, Q13, Q14, Q15, Q16, Q17, Q18, Q19, Q20, Q21, Q22, Q23, Q24, Q25, Q26, Q27, Q28, Q29, Q30, Q31]), "scope" : qUnion([Q32])});
        }
        {
            var Q0;
            Q0=makeQuery(id+"F31.opExtrude","SWEPT_FACE",FACE,{"disambiguationData":[OSD([sQuery(id+"F30.wireOp",EDGE,"E66.bottom")])]});
            var sketch = newSketch(context, id + "F37", { "sketchPlane" : qUnion([Q0])});
            skPoint(sketch, "E100", {"position": v(37.47, 4) * mm});
            skPoint(sketch, "E101", {"position": v(37.47, 2) * mm});
            skPoint(sketch, "E102", {"position": v(37.52, 11.5) * mm});
            skPoint(sketch, "E103", {"position": v(37.47, 9.5) * mm});
            skPoint(sketch, "E104", {"position": v(37.52, 19) * mm});
            skPoint(sketch, "E105", {"position": v(37.52, 17) * mm});
            skPoint(sketch, "E106", {"position": v(37.56, 26.5) * mm});
            skPoint(sketch, "E107", {"position": v(37.56, 24.5) * mm});
            skPoint(sketch, "E108", {"position": v(37.56, 34) * mm});
            skPoint(sketch, "E109", {"position": v(37.56, 32) * mm});
            skPoint(sketch, "E110", {"position": v(37.6, 41.5) * mm});
            skPoint(sketch, "E111", {"position": v(37.6, 39.5) * mm});
            skPoint(sketch, "E112", {"position": v(37.6, 49) * mm});
            skPoint(sketch, "E113", {"position": v(37.6, 47) * mm});
            skPoint(sketch, "E114", {"position": v(37.63, 56.5) * mm});
            skPoint(sketch, "E115", {"position": v(37.63, 54.5) * mm});
            skPoint(sketch, "E116", {"position": v(37.63, 64) * mm});
            skPoint(sketch, "E117", {"position": v(37.63, 62) * mm});
            skPoint(sketch, "E118", {"position": v(37.67, 71.5) * mm});
            skPoint(sketch, "E119", {"position": v(37.63, 69.5) * mm});
            skPoint(sketch, "E120", {"position": v(37.67, 79) * mm});
            skPoint(sketch, "E121", {"position": v(37.67, 77) * mm});
            skPoint(sketch, "E122", {"position": v(37.7, 86.5) * mm});
            skPoint(sketch, "E123", {"position": v(37.7, 84.5) * mm});
            skPoint(sketch, "E124", {"position": v(37.7, 94) * mm});
            skPoint(sketch, "E125", {"position": v(37.7, 92) * mm});
            skPoint(sketch, "E126", {"position": v(37.74, 101.5) * mm});
            skPoint(sketch, "E127", {"position": v(37.74, 99.5) * mm});
            skPoint(sketch, "E128", {"position": v(37.74, 109) * mm});
            skPoint(sketch, "E129", {"position": v(37.74, 107) * mm});
            skPoint(sketch, "E130", {"position": v(37.78, 116.5) * mm});
            skPoint(sketch, "E131", {"position": v(37.78, 114.5) * mm});
            skSolve(sketch);
        }
        {
            var Q0;
            Q0=sQuery(id+"F37.wireOp",VERTEX,"E130");
            var Q1;
            Q1=sQuery(id+"F37.wireOp",VERTEX,"E131");
            var Q2;
            Q2=sQuery(id+"F37.wireOp",VERTEX,"E128");
            var Q3;
            Q3=sQuery(id+"F37.wireOp",VERTEX,"E129");
            var Q4;
            Q4=sQuery(id+"F37.wireOp",VERTEX,"E126");
            var Q5;
            Q5=sQuery(id+"F37.wireOp",VERTEX,"E127");
            var Q6;
            Q6=sQuery(id+"F37.wireOp",VERTEX,"E125");
            var Q7;
            Q7=sQuery(id+"F37.wireOp",VERTEX,"E124");
            var Q8;
            Q8=sQuery(id+"F37.wireOp",VERTEX,"E122");
            var Q9;
            Q9=sQuery(id+"F37.wireOp",VERTEX,"E123");
            var Q10;
            Q10=sQuery(id+"F37.wireOp",VERTEX,"E120");
            var Q11;
            Q11=sQuery(id+"F37.wireOp",VERTEX,"E121");
            var Q12;
            Q12=sQuery(id+"F37.wireOp",VERTEX,"E118");
            var Q13;
            Q13=sQuery(id+"F37.wireOp",VERTEX,"E119");
            var Q14;
            Q14=sQuery(id+"F37.wireOp",VERTEX,"E116");
            var Q15;
            Q15=sQuery(id+"F37.wireOp",VERTEX,"E117");
            var Q16;
            Q16=sQuery(id+"F37.wireOp",VERTEX,"E114");
            var Q17;
            Q17=sQuery(id+"F37.wireOp",VERTEX,"E115");
            var Q18;
            Q18=sQuery(id+"F37.wireOp",VERTEX,"E112");
            var Q19;
            Q19=sQuery(id+"F37.wireOp",VERTEX,"E113");
            var Q20;
            Q20=sQuery(id+"F37.wireOp",VERTEX,"E110");
            var Q21;
            Q21=sQuery(id+"F37.wireOp",VERTEX,"E111");
            var Q22;
            Q22=sQuery(id+"F37.wireOp",VERTEX,"E108");
            var Q23;
            Q23=sQuery(id+"F37.wireOp",VERTEX,"E109");
            var Q24;
            Q24=sQuery(id+"F37.wireOp",VERTEX,"E106");
            var Q25;
            Q25=sQuery(id+"F37.wireOp",VERTEX,"E107");
            var Q26;
            Q26=sQuery(id+"F37.wireOp",VERTEX,"E104");
            var Q27;
            Q27=sQuery(id+"F37.wireOp",VERTEX,"E105");
            var Q28;
            Q28=sQuery(id+"F37.wireOp",VERTEX,"E102");
            var Q29;
            Q29=sQuery(id+"F37.wireOp",VERTEX,"E103");
            var Q30;
            Q30=sQuery(id+"F37.wireOp",VERTEX,"E100");
            var Q31;
            Q31=sQuery(id+"F37.wireOp",VERTEX,"E101");
            var Q32;
            Q32=makeQuery(id+"F31.opExtrude","SWEPT_BODY",BODY,{"disambiguationData":[OSD([sQuery(id+"F30.wireOp",EDGE,"E62.bottom"),sQuery(id+"F30.wireOp",EDGE,"E62.left"),sQuery(id+"F30.wireOp",EDGE,"E62.right"),sQuery(id+"F30.wireOp",EDGE,"E63.bottom"),sQuery(id+"F30.wireOp",EDGE,"E63.left"),sQuery(id+"F30.wireOp",EDGE,"E63.right"),sQuery(id+"F30.wireOp",EDGE,"E64.bottom"),sQuery(id+"F30.wireOp",EDGE,"E64.top"),sQuery(id+"F30.wireOp",EDGE,"E64.left"),sQuery(id+"F30.wireOp",EDGE,"E64.right"),sQuery(id+"F30.wireOp",EDGE,"E65.bottom"),sQuery(id+"F30.wireOp",EDGE,"E65.top"),sQuery(id+"F30.wireOp",EDGE,"E65.right"),sQuery(id+"F30.wireOp",EDGE,"E66.bottom"),sQuery(id+"F30.wireOp",EDGE,"E66.top"),sQuery(id+"F30.wireOp",EDGE,"E66.left")])]});
            hole(context, id + "F38", {"style" : HoleStyle.SIMPLE, "endStyle" : HoleEndStyle.BLIND, "holeDiameter" : .8 * mm, "majorDiameter" : 5 * mm, "holeDepth" : 2 * mm, "isTappedThrough" : true, "tappedDepth" : 12 * mm, "tapClearance" : 3, "locations" : qUnion([Q0, Q1, Q2, Q3, Q4, Q5, Q6, Q7, Q8, Q9, Q10, Q11, Q12, Q13, Q14, Q15, Q16, Q17, Q18, Q19, Q20, Q21, Q22, Q23, Q24, Q25, Q26, Q27, Q28, Q29, Q30, Q31]), "scope" : qUnion([Q32])});
        }
    });
